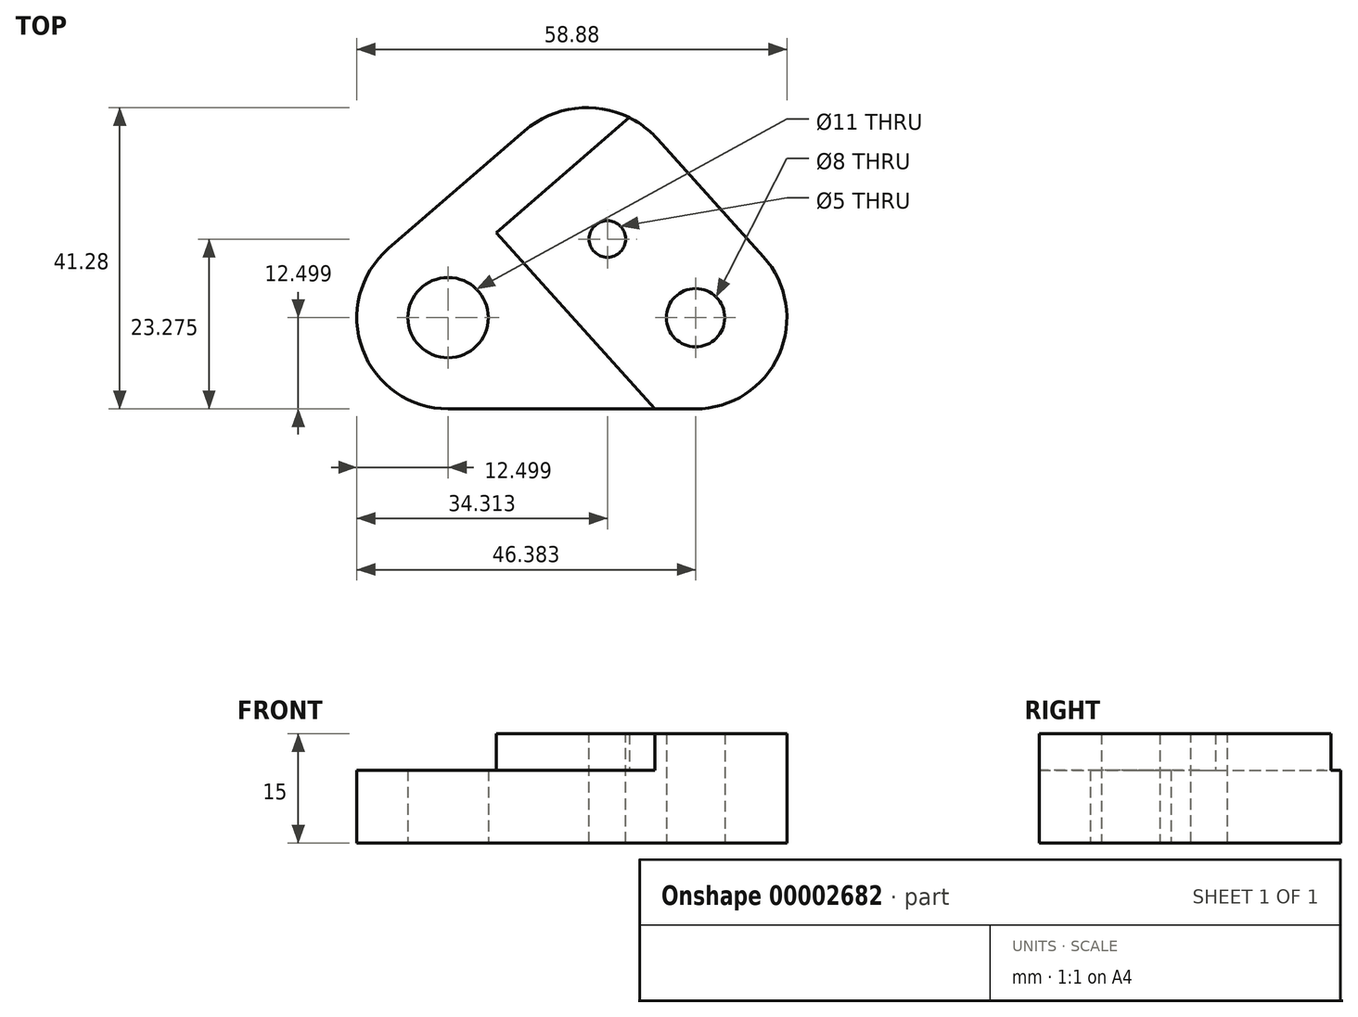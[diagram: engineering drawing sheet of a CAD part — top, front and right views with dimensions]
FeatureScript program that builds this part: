
annotation { "Feature Type Name" : "Feature", "Feature Type Description" : "" }
export const myFeature = defineFeature(function(context is Context, id is Id, definition is map)
    precondition{}
    {
        {
            var Q0;
            Q0=qCreatedBy(makeId("Top.planeOp"),FACE);
            var sketch = newSketch(context, id + "F0", { "sketchPlane" : qUnion([Q0])});
            skPoint(sketch, "E0.visualSharp", {"position": v(0.86, 31.66) * mm});
            skArc(sketch, "E0.filletArc", {"start": v(9.39, 22.18) * mm, "mid": v(0.54, 26.46) * mm, "end": v(-8.78, 23.31) * mm});
            skLineSegment(sketch, "E1", {"start": v(23.9, 6.06) * mm, "end": v(9.39, 22.18) * mm});
            skPoint(sketch, "E2.visualSharp", {"position": v(-52.83, -14.8) * mm});
            skArc(sketch, "E2.filletArc", {"start": v(-27.46, 7.15) * mm, "mid": v(-31, -6.66) * mm, "end": v(-19.28, -14.8) * mm});
            skLineSegment(sketch, "E3", {"start": v(-19.28, -14.8) * mm, "end": v(14.6, -14.8) * mm});
            skPoint(sketch, "E4.visualSharp", {"position": v(42.67, -14.8) * mm});
            skArc(sketch, "E4.filletArc", {"start": v(14.6, -14.8) * mm, "mid": v(26.02, -7.39) * mm, "end": v(23.9, 6.06) * mm});
            skLineSegment(sketch, "E5", {"start": v(-27.46, 7.15) * mm, "end": v(-8.78, 23.31) * mm});
            skPoint(sketch, "E6.trimOffspring.end.orphan", {"position": v(0, 32.61) * mm});
            skArc(sketch, "E7.0", {"start": v(-24.43, -4.22) * mm, "mid": v(-22.42, -6.82) * mm, "end": v(-19.28, -7.8) * mm});
            skCircle(sketch, "E8", {"center": v(-19.28, -2.3) * mm, "radius": 5.5 * mm});
            skCircle(sketch, "E9", {"center": v(14.6, -2.3) * mm, "radius": 4 * mm});
            skSolve(sketch);
        }
        {
            var Q0;
            Q0=makeQuery(id+"F0.imprint","IMPRINT",FACE,{"disambiguationData":[TD([[makeQuery(id+"F0.imprint","IMPRINT",EDGE,{"derivedFrom":sQuery(id+"F0.wireOp",EDGE,"E0.filletArc")}),1.0]])]});
            extrude(context, id + "F1", {"entities" : qUnion([Q0]), "depth" : 10 * mm});
        }
        {
            var Q0;
            Q0=makeQuery(id+"F1.opExtrude","CAP_FACE",FACE,{"disambiguationData":[OSD([sQuery(id+"F0.wireOp",EDGE,"E0.filletArc"),sQuery(id+"F0.wireOp",EDGE,"E1"),sQuery(id+"F0.wireOp",EDGE,"E2.filletArc"),sQuery(id+"F0.wireOp",EDGE,"E3"),sQuery(id+"F0.wireOp",EDGE,"E4.filletArc"),sQuery(id+"F0.wireOp",EDGE,"E5"),sQuery(id+"F0.wireOp",EDGE,"E8"),sQuery(id+"F0.wireOp",EDGE,"E9")])],"isStart":false});
            var sketch = newSketch(context, id + "F2", { "sketchPlane" : qUnion([Q0])});
            skLineSegment(sketch, "E10", {"start": v(9.82, -15.67) * mm, "end": v(-12.7, 9.35) * mm});
            skLineSegment(sketch, "E11.0", {"start": v(-12.7, 9.35) * mm, "end": v(7.35, 26.7) * mm});
            skSolve(sketch);
        }
        {
            var Q0;
            Q0 = qSketchRegion(id + "F2", true);
            var Q1;
            {var subQ7=makeQuery(id+"F1.opExtrude","CAP_EDGE",EDGE,{"disambiguationData":[OSD([sQuery(id+"F0.wireOp",EDGE,"E1")])],"isStart":false});Q1=makeQuery(id+"F2.imprint","IMPRINT",FACE,{"disambiguationData":[TD([[makeQuery(id+"F2.imprint","IMPRINT",EDGE,{"derivedFrom":subQ7}),1.0]])]});}
            extrude(context, id + "F3", {"entities" : qUnion([Q0, Q1]), "operationType" : NewBodyOperationType.ADD, "depth" : 5 * mm});
        }
        {
            var Q0;
            Q0=makeQuery(id+"F3.opExtrude","CAP_FACE",FACE,{"disambiguationData":[OSD([sQuery(id+"F0.wireOp",EDGE,"E0.filletArc"),sQuery(id+"F0.wireOp",EDGE,"E1"),sQuery(id+"F0.wireOp",EDGE,"E3"),sQuery(id+"F0.wireOp",EDGE,"E4.filletArc"),sQuery(id+"F0.wireOp",EDGE,"E9"),sQuery(id+"F2.wireOp",EDGE,"E10"),sQuery(id+"F2.wireOp",EDGE,"E11.0")])],"isStart":false});
            var sketch = newSketch(context, id + "F4", { "sketchPlane" : qUnion([Q0])});
            skCircle(sketch, "E12", {"center": v(2.53, 8.48) * mm, "radius": 2.5 * mm});
            skSolve(sketch);
        }
        {
            var Q0;
            Q0=makeQuery(id+"F4.imprint","IMPRINT",FACE,{"disambiguationData":[TD([[makeQuery(id+"F4.imprint","IMPRINT",EDGE,{"derivedFrom":sQuery(id+"F4.wireOp",EDGE,"E12")}),1.0]])]});
            var Q1;
            Q1=makeQuery(id+"F1.opExtrude","CAP_FACE",FACE,{"disambiguationData":[OSD([sQuery(id+"F0.wireOp",EDGE,"E0.filletArc"),sQuery(id+"F0.wireOp",EDGE,"E1"),sQuery(id+"F0.wireOp",EDGE,"E2.filletArc"),sQuery(id+"F0.wireOp",EDGE,"E3"),sQuery(id+"F0.wireOp",EDGE,"E4.filletArc"),sQuery(id+"F0.wireOp",EDGE,"E5"),sQuery(id+"F0.wireOp",EDGE,"E8"),sQuery(id+"F0.wireOp",EDGE,"E9")])],"isStart":true});
            extrude(context, id + "F5", {"entities" : qUnion([Q0]), "operationType" : NewBodyOperationType.REMOVE, "oppositeDirection" : true, "endBoundEntityFace" : qUnion([Q1]), "depth" : 15 * mm});
        }
    });
